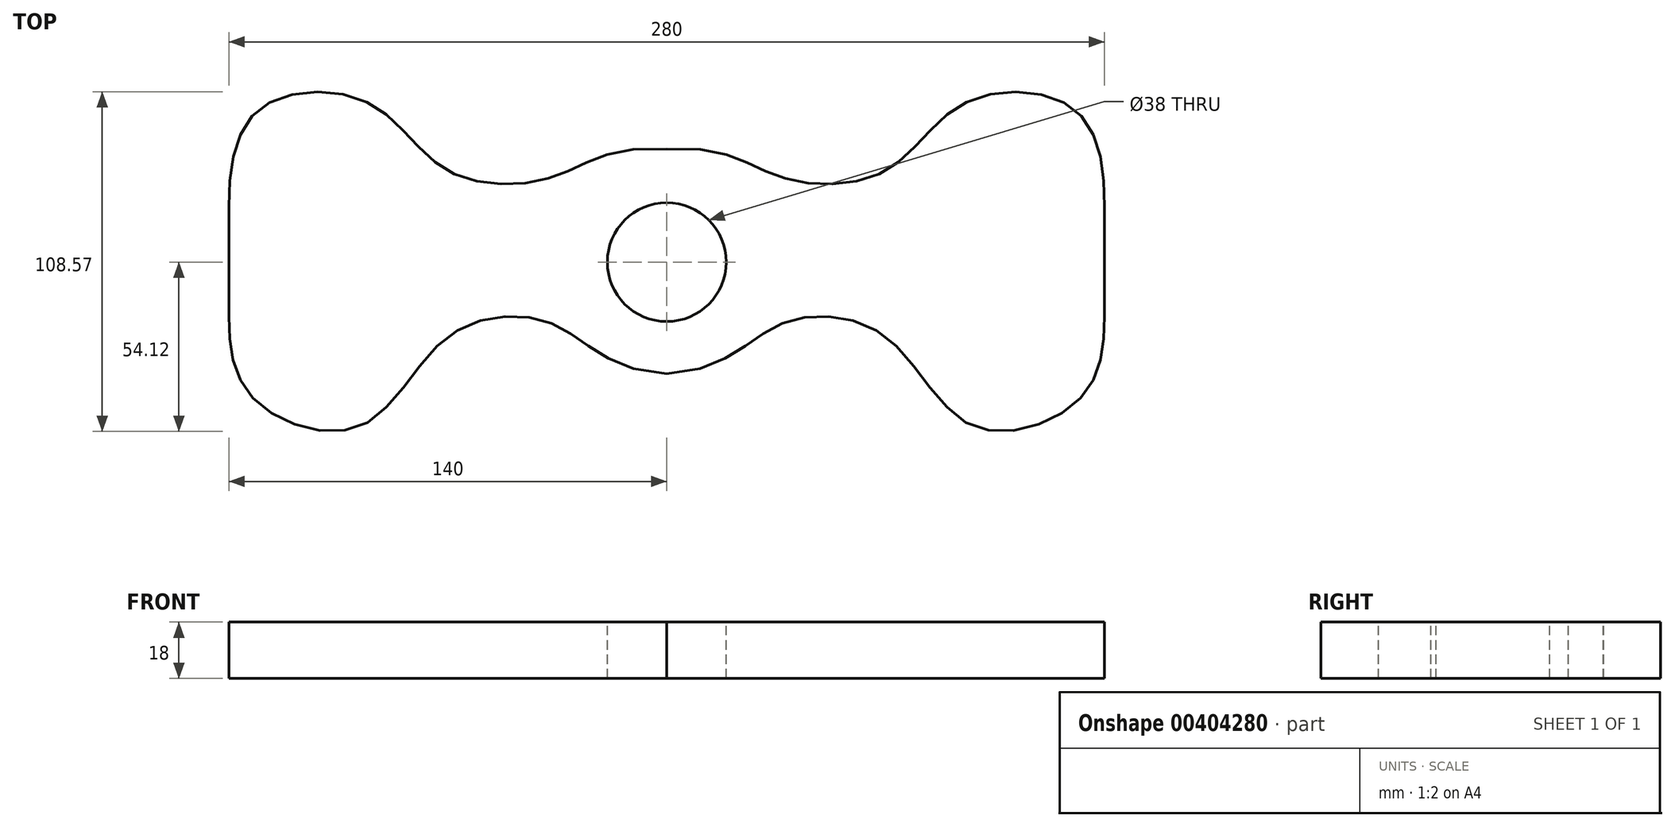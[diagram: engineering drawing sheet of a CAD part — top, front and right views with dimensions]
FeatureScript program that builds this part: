
annotation { "Feature Type Name" : "Feature", "Feature Type Description" : "" }
export const myFeature = defineFeature(function(context is Context, id is Id, definition is map)
    precondition{}
    {
        {
            var Q0;
            Q0=qCreatedBy(makeId("Top.planeOp"),FACE);
            var sketch = newSketch(context, id + "F0", { "sketchPlane" : qUnion([Q0])});
            skLineSegment(sketch, "E0.bottom", {"start": v(0, 0) * mm, "end": v(280, 0) * mm});
            skLineSegment(sketch, "E0.top", {"start": v(0, 145) * mm, "end": v(280, 145) * mm});
            skLineSegment(sketch, "E0.left", {"start": v(0, 0) * mm, "end": v(0, 145) * mm});
            skLineSegment(sketch, "E0.right", {"start": v(280, 0) * mm, "end": v(280, 145) * mm});
            skSolve(sketch);
        }
        {
            var Q0;
            Q0 = qSketchRegion(id + "F0", true);
            extrude(context, id + "F1", {"entities" : qUnion([Q0]), "depth" : 18 * mm});
        }
        {
            var Q0;
            Q0=makeQuery(id+"F1.opExtrude","CAP_FACE",FACE,{"disambiguationData":[OSD([sQuery(id+"F0.wireOp",EDGE,"E0.bottom"),sQuery(id+"F0.wireOp",EDGE,"E0.top"),sQuery(id+"F0.wireOp",EDGE,"E0.left"),sQuery(id+"F0.wireOp",EDGE,"E0.right")])],"isStart":false});
            var sketch = newSketch(context, id + "F2", { "sketchPlane" : qUnion([Q0])});
            skCircle(sketch, "E1", {"center": v(140, 72.5) * mm, "radius": 19 * mm});
            skPoint(sketch, "E1.centerSnap1", {"position": v(140, 145) * mm});
            skArc(sketch, "E2", {"start": v(49.34, 68.36) * mm, "mid": v(46.05, 78.4) * mm, "end": v(39.5, 70.11) * mm});
            skPoint(sketch, "E2.centerSnap0", {"position": v(0, 72.5) * mm});
            skFitSpline(sketch, "E3", {"points": [v(0, 72.5) * mm, v(11.9, 85.67) * mm, v(19.52, 105.99) * mm, v(33.9, 103.41) * mm, v(24.3, 69.12) * mm, v(17.21, 42.57) * mm, v(29.78, 38.12) * mm, v(45, 72.5) * mm], "startDerivative": vector(268.1, -30.18) * mm, "endDerivative": vector(48.17, 283.04) * mm, "construction": true});
            skLineSegment(sketch, "E4", {"start": v(0, 107.5) * mm, "end": v(57, 107.5) * mm, "construction": true});
            skLineSegment(sketch, "E5", {"start": v(0, 37.5) * mm, "end": v(64.72, 37.5) * mm, "construction": true});
            skFitSpline(sketch, "E6.0", {"points": [v(-0.56, 67.53) * mm, v(1.1, 67.34) * mm, v(3.4, 67.28) * mm, v(6.24, 67.67) * mm, v(8.26, 68.24) * mm, v(10.13, 69.13) * mm, v(11.8, 70.3) * mm, v(13.17, 71.71) * mm, v(14.24, 73.26) * mm, v(15.03, 74.84) * mm, v(15.79, 76.95) * mm, v(16.22, 79) * mm, v(16.49, 80.98) * mm, v(16.64, 82.44) * mm, v(16.74, 83.62) * mm, v(16.82, 84.55) * mm, v(16.88, 85.23) * mm, v(16.94, 85.9) * mm, v(17.02, 86.8) * mm, v(17.14, 87.92) * mm, v(17.3, 89.24) * mm, v(17.53, 90.97) * mm, v(17.88, 93.04) * mm, v(18.4, 95.34) * mm, v(19.05, 97.36) * mm, v(19.79, 99.05) * mm, v(20.45, 100.13) * mm, v(21, 100.8) * mm, v(21.4, 101.2) * mm, v(21.73, 101.47) * mm, v(22, 101.65) * mm, v(22.28, 101.82) * mm, v(22.69, 102.01) * mm, v(23.44, 102.28) * mm, v(24.54, 102.5) * mm, v(25.96, 102.52) * mm, v(27.32, 102.29) * mm, v(28.26, 101.93) * mm, v(28.84, 101.6) * mm, v(29.17, 101.35) * mm, v(29.42, 101.1) * mm, v(29.56, 100.92) * mm, v(29.64, 100.78) * mm, v(29.73, 100.6) * mm, v(29.84, 100.31) * mm, v(29.96, 99.8) * mm, v(30.06, 98.92) * mm, v(30.04, 97.43) * mm, v(29.69, 95.14) * mm, v(29, 92.48) * mm, v(28.04, 89.54) * mm, v(26.83, 86.39) * mm, v(24.95, 82) * mm, v(22.8, 77.42) * mm, v(20.56, 72.85) * mm, v(18.35, 68.35) * mm, v(16.25, 63.99) * mm, v(14.41, 59.77) * mm, v(13.22, 56.68) * mm, v(12.24, 53.64) * mm, v(11.54, 50.63) * mm, v(11.19, 47.61) * mm, v(11.3, 45.05) * mm, v(11.7, 43) * mm, v(12.1, 41.73) * mm, v(12.54, 40.73) * mm, v(13.03, 39.76) * mm, v(13.76, 38.62) * mm, v(14.77, 37.4) * mm, v(16.26, 35.96) * mm, v(18.36, 34.5) * mm, v(21.15, 33.26) * mm, v(24.14, 32.55) * mm, v(26.76, 32.44) * mm, v(28.88, 32.69) * mm, v(30.2, 33) * mm, v(31.26, 33.33) * mm, v(32.3, 33.74) * mm, v(33.54, 34.35) * mm, v(34.92, 35.24) * mm, v(36.62, 36.6) * mm, v(38.5, 38.55) * mm, v(40.44, 41.24) * mm, v(42.13, 44.22) * mm, v(43.63, 47.47) * mm, v(44.97, 50.98) * mm, v(46.58, 55.98) * mm, v(48.3, 62.77) * mm, v(49.42, 68.65) * mm, v(49.93, 71.66) * mm]});
            skFitSpline(sketch, "E7.0", {"points": [v(-0.56, 67.53) * mm, v(1.1, 67.34) * mm, v(3.4, 67.28) * mm, v(6.24, 67.67) * mm, v(8.26, 68.24) * mm, v(10.13, 69.13) * mm, v(11.8, 70.3) * mm, v(13.17, 71.71) * mm, v(14.24, 73.26) * mm, v(15.03, 74.84) * mm, v(15.79, 76.95) * mm, v(16.22, 79) * mm, v(16.49, 80.98) * mm, v(16.64, 82.44) * mm, v(16.74, 83.62) * mm, v(16.82, 84.55) * mm, v(16.88, 85.23) * mm, v(16.94, 85.9) * mm, v(17.02, 86.8) * mm, v(17.14, 87.92) * mm, v(17.3, 89.24) * mm, v(17.53, 90.97) * mm, v(17.88, 93.04) * mm, v(18.4, 95.34) * mm, v(19.05, 97.36) * mm, v(19.79, 99.05) * mm, v(20.45, 100.13) * mm, v(21, 100.8) * mm, v(21.4, 101.2) * mm, v(21.73, 101.47) * mm, v(22, 101.65) * mm, v(22.28, 101.82) * mm, v(22.69, 102.01) * mm, v(23.44, 102.28) * mm, v(24.54, 102.5) * mm, v(25.96, 102.52) * mm, v(27.32, 102.29) * mm, v(28.26, 101.93) * mm, v(28.84, 101.6) * mm, v(29.17, 101.35) * mm, v(29.42, 101.1) * mm, v(29.56, 100.92) * mm, v(29.64, 100.78) * mm, v(29.73, 100.6) * mm, v(29.84, 100.31) * mm, v(29.96, 99.8) * mm, v(30.06, 98.92) * mm, v(30.04, 97.43) * mm, v(29.69, 95.14) * mm, v(29, 92.48) * mm, v(28.04, 89.54) * mm, v(26.83, 86.39) * mm, v(24.95, 82) * mm, v(22.8, 77.42) * mm, v(20.56, 72.85) * mm, v(18.35, 68.35) * mm, v(16.25, 63.99) * mm, v(14.41, 59.77) * mm, v(13.22, 56.68) * mm, v(12.24, 53.64) * mm, v(11.54, 50.63) * mm, v(11.19, 47.61) * mm, v(11.3, 45.05) * mm, v(11.7, 43) * mm, v(12.1, 41.73) * mm, v(12.54, 40.73) * mm, v(13.03, 39.76) * mm, v(13.76, 38.62) * mm, v(14.77, 37.4) * mm, v(16.26, 35.96) * mm, v(18.36, 34.5) * mm, v(21.15, 33.26) * mm, v(24.14, 32.55) * mm, v(26.76, 32.44) * mm, v(28.88, 32.69) * mm, v(30.2, 33) * mm, v(31.26, 33.33) * mm, v(32.3, 33.74) * mm, v(33.54, 34.35) * mm, v(34.92, 35.24) * mm, v(36.62, 36.6) * mm, v(38.5, 38.55) * mm, v(40.44, 41.24) * mm, v(42.13, 44.22) * mm, v(43.63, 47.47) * mm, v(44.97, 50.98) * mm, v(46.58, 55.98) * mm, v(48.3, 62.77) * mm, v(49.42, 68.65) * mm, v(49.93, 71.66) * mm]});
            skFitSpline(sketch, "E8.0", {"points": [v(0.56, 77.47) * mm, v(1.7, 77.34) * mm, v(3.07, 77.32) * mm, v(4.21, 77.5) * mm, v(4.77, 77.66) * mm, v(5.09, 77.82) * mm, v(5.27, 77.95) * mm, v(5.42, 78.1) * mm, v(5.6, 78.35) * mm, v(5.8, 78.75) * mm, v(6.1, 79.54) * mm, v(6.36, 80.7) * mm, v(6.56, 82.15) * mm, v(6.68, 83.36) * mm, v(6.78, 84.46) * mm, v(6.85, 85.38) * mm, v(6.91, 86.09) * mm, v(6.98, 86.81) * mm, v(7.07, 87.78) * mm, v(7.2, 89) * mm, v(7.37, 90.49) * mm, v(7.64, 92.47) * mm, v(8.06, 94.96) * mm, v(8.73, 97.92) * mm, v(9.64, 100.81) * mm, v(10.85, 103.6) * mm, v(12.19, 105.81) * mm, v(13.52, 107.45) * mm, v(14.65, 108.6) * mm, v(15.71, 109.47) * mm, v(16.64, 110.1) * mm, v(17.6, 110.67) * mm, v(18.85, 111.27) * mm, v(20.4, 111.81) * mm, v(21.96, 112.2) * mm, v(24.07, 112.5) * mm, v(26.72, 112.54) * mm, v(29.86, 112.02) * mm, v(32.38, 111.1) * mm, v(34.3, 110) * mm, v(35.65, 109) * mm, v(36.9, 107.8) * mm, v(37.8, 106.62) * mm, v(38.43, 105.57) * mm, v(38.96, 104.5) * mm, v(39.47, 103.11) * mm, v(39.85, 101.44) * mm, v(40.1, 99.2) * mm, v(40.02, 96.41) * mm, v(39.48, 93.05) * mm, v(38.6, 89.63) * mm, v(37.45, 86.14) * mm, v(36.09, 82.6) * mm, v(34.05, 77.84) * mm, v(31.8, 73.07) * mm, v(29.53, 68.44) * mm, v(27.88, 65.08) * mm, v(26.32, 61.86) * mm, v(24.42, 57.8) * mm, v(22.89, 54.1) * mm, v(21.87, 50.92) * mm, v(21.4, 48.85) * mm, v(21.22, 47.15) * mm, v(21.28, 46.11) * mm, v(21.4, 45.5) * mm, v(21.5, 45.2) * mm, v(21.6, 44.98) * mm, v(21.7, 44.8) * mm, v(21.85, 44.54) * mm, v(22.12, 44.22) * mm, v(22.56, 43.79) * mm, v(23.29, 43.27) * mm, v(24.36, 42.8) * mm, v(25.53, 42.52) * mm, v(26.48, 42.48) * mm, v(27.18, 42.56) * mm, v(27.6, 42.66) * mm, v(27.9, 42.76) * mm, v(28.2, 42.87) * mm, v(28.58, 43.06) * mm, v(29.08, 43.38) * mm, v(29.79, 43.94) * mm, v(30.76, 44.93) * mm, v(31.98, 46.6) * mm, v(33.2, 48.75) * mm, v(34.79, 52.18) * mm, v(36.62, 57.42) * mm, v(38.51, 64.9) * mm, v(39.58, 70.46) * mm, v(40.07, 73.34) * mm]});
            skLineSegment(sketch, "E9.trimOffspring", {"start": v(0, 67.47) * mm, "end": v(0, 77.54) * mm});
            skLineSegment(sketch, "E10", {"start": v(0.56, 77.47) * mm, "end": v(0, 77.54) * mm});
            skLineSegment(sketch, "E11", {"start": v(140, 145) * mm, "end": v(140, 0) * mm, "construction": true});
            skLineSegment(sketch, "E12.MirrorCS", {"start": v(279.44, 77.47) * mm, "end": v(280, 77.54) * mm});
            skLineSegment(sketch, "E13.MirrorCS", {"start": v(280, 67.47) * mm, "end": v(280, 77.54) * mm});
            skPoint(sketch, "E14.MirrorP", {"position": v(280, 72.5) * mm});
            skLineSegment(sketch, "E15.MirrorCS", {"start": v(280, 107.5) * mm, "end": v(223, 107.5) * mm, "construction": true});
            skLineSegment(sketch, "E16.MirrorCS", {"start": v(280, 37.5) * mm, "end": v(215.28, 37.5) * mm, "construction": true});
            skFitSpline(sketch, "E17.MirrorCS", {"points": [v(280, 72.5) * mm, v(268.1, 85.67) * mm, v(260.48, 105.99) * mm, v(246.1, 103.41) * mm, v(255.7, 69.12) * mm, v(262.79, 42.57) * mm, v(250.22, 38.12) * mm, v(235, 72.5) * mm], "startDerivative": vector(-268.1, -30.18) * mm, "endDerivative": vector(-48.17, 283.04) * mm, "construction": true});
            skLineSegment(sketch, "E18.MirrorCS", {"start": v(280, 0) * mm, "end": v(280, 37.5) * mm});
            skArc(sketch, "E19.MirrorCS", {"start": v(230.66, 68.36) * mm, "mid": v(233.95, 78.4) * mm, "end": v(240.5, 70.11) * mm});
            skFitSpline(sketch, "E20.0", {"points": [v(279.44, 77.47) * mm, v(278.3, 77.34) * mm, v(276.93, 77.32) * mm, v(275.79, 77.5) * mm, v(275.23, 77.66) * mm, v(274.91, 77.82) * mm, v(274.73, 77.95) * mm, v(274.58, 78.1) * mm, v(274.4, 78.35) * mm, v(274.2, 78.75) * mm, v(273.9, 79.54) * mm, v(273.64, 80.7) * mm, v(273.44, 82.15) * mm, v(273.32, 83.36) * mm, v(273.22, 84.46) * mm, v(273.15, 85.38) * mm, v(273.09, 86.09) * mm, v(273.02, 86.81) * mm, v(272.93, 87.78) * mm, v(272.8, 89) * mm, v(272.63, 90.49) * mm, v(272.36, 92.47) * mm, v(271.94, 94.96) * mm, v(271.27, 97.92) * mm, v(270.36, 100.81) * mm, v(269.15, 103.6) * mm, v(267.81, 105.81) * mm, v(266.48, 107.45) * mm, v(265.35, 108.6) * mm, v(264.29, 109.47) * mm, v(263.36, 110.1) * mm, v(262.4, 110.67) * mm, v(261.15, 111.27) * mm, v(259.6, 111.81) * mm, v(258.04, 112.2) * mm, v(255.93, 112.5) * mm, v(253.28, 112.54) * mm, v(250.14, 112.02) * mm, v(247.62, 111.1) * mm, v(245.7, 110) * mm, v(244.35, 109) * mm, v(243.1, 107.8) * mm, v(242.2, 106.62) * mm, v(241.57, 105.57) * mm, v(241.04, 104.5) * mm, v(240.53, 103.11) * mm, v(240.15, 101.44) * mm, v(239.9, 99.2) * mm, v(239.98, 96.41) * mm, v(240.52, 93.05) * mm, v(241.4, 89.63) * mm, v(242.55, 86.14) * mm, v(243.91, 82.6) * mm, v(245.95, 77.84) * mm, v(248.2, 73.07) * mm, v(250.47, 68.44) * mm, v(252.12, 65.08) * mm, v(253.68, 61.86) * mm, v(255.58, 57.8) * mm, v(257.11, 54.1) * mm, v(258.13, 50.92) * mm, v(258.6, 48.85) * mm, v(258.78, 47.15) * mm, v(258.72, 46.11) * mm, v(258.6, 45.5) * mm, v(258.5, 45.2) * mm, v(258.4, 44.98) * mm, v(258.3, 44.8) * mm, v(258.15, 44.54) * mm, v(257.88, 44.22) * mm, v(257.44, 43.79) * mm, v(256.71, 43.27) * mm, v(255.64, 42.8) * mm, v(254.47, 42.52) * mm, v(253.52, 42.48) * mm, v(252.82, 42.56) * mm, v(252.4, 42.66) * mm, v(252.1, 42.76) * mm, v(251.8, 42.87) * mm, v(251.42, 43.06) * mm, v(250.92, 43.38) * mm, v(250.21, 43.94) * mm, v(249.24, 44.93) * mm, v(248.02, 46.6) * mm, v(246.8, 48.75) * mm, v(245.21, 52.18) * mm, v(243.38, 57.42) * mm, v(241.49, 64.9) * mm, v(240.42, 70.46) * mm, v(239.93, 73.34) * mm]});
            skFitSpline(sketch, "E21.0", {"points": [v(280.56, 67.53) * mm, v(278.9, 67.34) * mm, v(276.6, 67.28) * mm, v(273.76, 67.67) * mm, v(271.74, 68.24) * mm, v(269.87, 69.13) * mm, v(268.2, 70.3) * mm, v(266.83, 71.71) * mm, v(265.76, 73.26) * mm, v(264.97, 74.84) * mm, v(264.21, 76.95) * mm, v(263.78, 79) * mm, v(263.51, 80.98) * mm, v(263.36, 82.44) * mm, v(263.26, 83.62) * mm, v(263.18, 84.55) * mm, v(263.12, 85.23) * mm, v(263.06, 85.9) * mm, v(262.98, 86.8) * mm, v(262.86, 87.92) * mm, v(262.7, 89.24) * mm, v(262.47, 90.97) * mm, v(262.12, 93.04) * mm, v(261.6, 95.34) * mm, v(260.95, 97.36) * mm, v(260.21, 99.05) * mm, v(259.55, 100.13) * mm, v(259, 100.8) * mm, v(258.6, 101.2) * mm, v(258.27, 101.47) * mm, v(258, 101.65) * mm, v(257.72, 101.82) * mm, v(257.31, 102.01) * mm, v(256.56, 102.28) * mm, v(255.46, 102.5) * mm, v(254.04, 102.52) * mm, v(252.68, 102.29) * mm, v(251.74, 101.93) * mm, v(251.16, 101.6) * mm, v(250.83, 101.35) * mm, v(250.58, 101.1) * mm, v(250.44, 100.92) * mm, v(250.36, 100.78) * mm, v(250.27, 100.6) * mm, v(250.16, 100.31) * mm, v(250.04, 99.8) * mm, v(249.94, 98.92) * mm, v(249.96, 97.43) * mm, v(250.31, 95.14) * mm, v(251, 92.48) * mm, v(251.96, 89.54) * mm, v(253.17, 86.39) * mm, v(255.05, 82) * mm, v(257.2, 77.42) * mm, v(259.44, 72.85) * mm, v(261.65, 68.35) * mm, v(263.75, 63.99) * mm, v(265.59, 59.77) * mm, v(266.78, 56.68) * mm, v(267.76, 53.64) * mm, v(268.46, 50.63) * mm, v(268.81, 47.61) * mm, v(268.7, 45.05) * mm, v(268.3, 43) * mm, v(267.9, 41.73) * mm, v(267.46, 40.73) * mm, v(266.97, 39.76) * mm, v(266.24, 38.62) * mm, v(265.23, 37.4) * mm, v(263.74, 35.96) * mm, v(261.64, 34.5) * mm, v(258.85, 33.26) * mm, v(255.86, 32.55) * mm, v(253.24, 32.44) * mm, v(251.12, 32.69) * mm, v(249.8, 33) * mm, v(248.74, 33.33) * mm, v(247.7, 33.74) * mm, v(246.46, 34.35) * mm, v(245.08, 35.24) * mm, v(243.38, 36.6) * mm, v(241.5, 38.55) * mm, v(239.56, 41.24) * mm, v(237.87, 44.22) * mm, v(236.37, 47.47) * mm, v(235.03, 50.98) * mm, v(233.42, 55.98) * mm, v(231.7, 62.77) * mm, v(230.58, 68.65) * mm, v(230.07, 71.66) * mm]});
            skSolve(sketch);
        }
        {
            var Q0;
            Q0 = qSketchRegion(id + "F2", true);
            extrude(context, id + "F3", {"entities" : qUnion([Q0]), "operationType" : NewBodyOperationType.REMOVE, "endBound" : BoundingType.THROUGH_ALL, "oppositeDirection" : true, "depth" : 25 * mm});
        }
        {
            var Q0;
            Q0=makeQuery(id+"F1.opExtrude","CAP_FACE",FACE,{"disambiguationData":[OSD([sQuery(id+"F0.wireOp",EDGE,"E0.bottom"),sQuery(id+"F0.wireOp",EDGE,"E0.top"),sQuery(id+"F0.wireOp",EDGE,"E0.left"),sQuery(id+"F0.wireOp",EDGE,"E0.right")])],"isStart":false});
            var sketch = newSketch(context, id + "F4", { "sketchPlane" : qUnion([Q0])});
            skLineSegment(sketch, "E22", {"start": v(140, 145) * mm, "end": v(140, 0) * mm, "construction": true});
            skPoint(sketch, "E23.centerSnap0", {"position": v(140, 72.5) * mm});
            skLineSegment(sketch, "E24", {"start": v(0, 145) * mm, "end": v(0, 0) * mm, "construction": true});
            skFitSpline(sketch, "E25", {"points": [v(0, 90.44) * mm, v(9.87, 121.43) * mm, v(44.98, 123.26) * mm, v(69.5, 102.04) * mm, v(103.11, 99.55) * mm, v(140, 108.67) * mm], "startDerivative": vector(0, 186.84) * mm, "endDerivative": vector(285.96, -19.85) * mm});
            skFitSpline(sketch, "E26", {"points": [v(0, 55.02) * mm, v(8.05, 28.71) * mm, v(42.17, 20.12) * mm, v(70.44, 49) * mm, v(103.91, 52.54) * mm, v(140, 36.79) * mm], "startDerivative": vector(0, -163.42) * mm, "endDerivative": vector(284.1, -16.1) * mm});
            skFitSpline(sketch, "E27.MirrorCS", {"points": [v(280, 90.44) * mm, v(270.13, 121.43) * mm, v(235.02, 123.26) * mm, v(210.5, 102.04) * mm, v(176.89, 99.55) * mm, v(140, 108.67) * mm], "startDerivative": vector(0, 186.84) * mm, "endDerivative": vector(-285.96, -19.85) * mm});
            skFitSpline(sketch, "E28.MirrorCS", {"points": [v(280, 55.02) * mm, v(271.95, 28.71) * mm, v(237.83, 20.12) * mm, v(209.56, 49) * mm, v(176.09, 52.54) * mm, v(140, 36.79) * mm], "startDerivative": vector(0, -163.42) * mm, "endDerivative": vector(-284.1, -16.1) * mm});
            skLineSegment(sketch, "E29", {"start": v(0, 90.44) * mm, "end": v(0, 145) * mm});
            skLineSegment(sketch, "E30", {"start": v(280, 145) * mm, "end": v(0, 145) * mm});
            skLineSegment(sketch, "E31", {"start": v(280, 145) * mm, "end": v(280, 90.44) * mm});
            skLineSegment(sketch, "E32", {"start": v(0, 55.02) * mm, "end": v(0, 0) * mm});
            skLineSegment(sketch, "E33", {"start": v(0, 0) * mm, "end": v(280, 0) * mm});
            skLineSegment(sketch, "E34", {"start": v(280, 0) * mm, "end": v(280, 55.02) * mm});
            skSolve(sketch);
        }
        {
            var Q0;
            Q0 = qSketchRegion(id + "F4", true);
            extrude(context, id + "F5", {"entities" : qUnion([Q0]), "operationType" : NewBodyOperationType.REMOVE, "endBound" : BoundingType.THROUGH_ALL, "oppositeDirection" : true, "depth" : 25 * mm});
        }
    });
